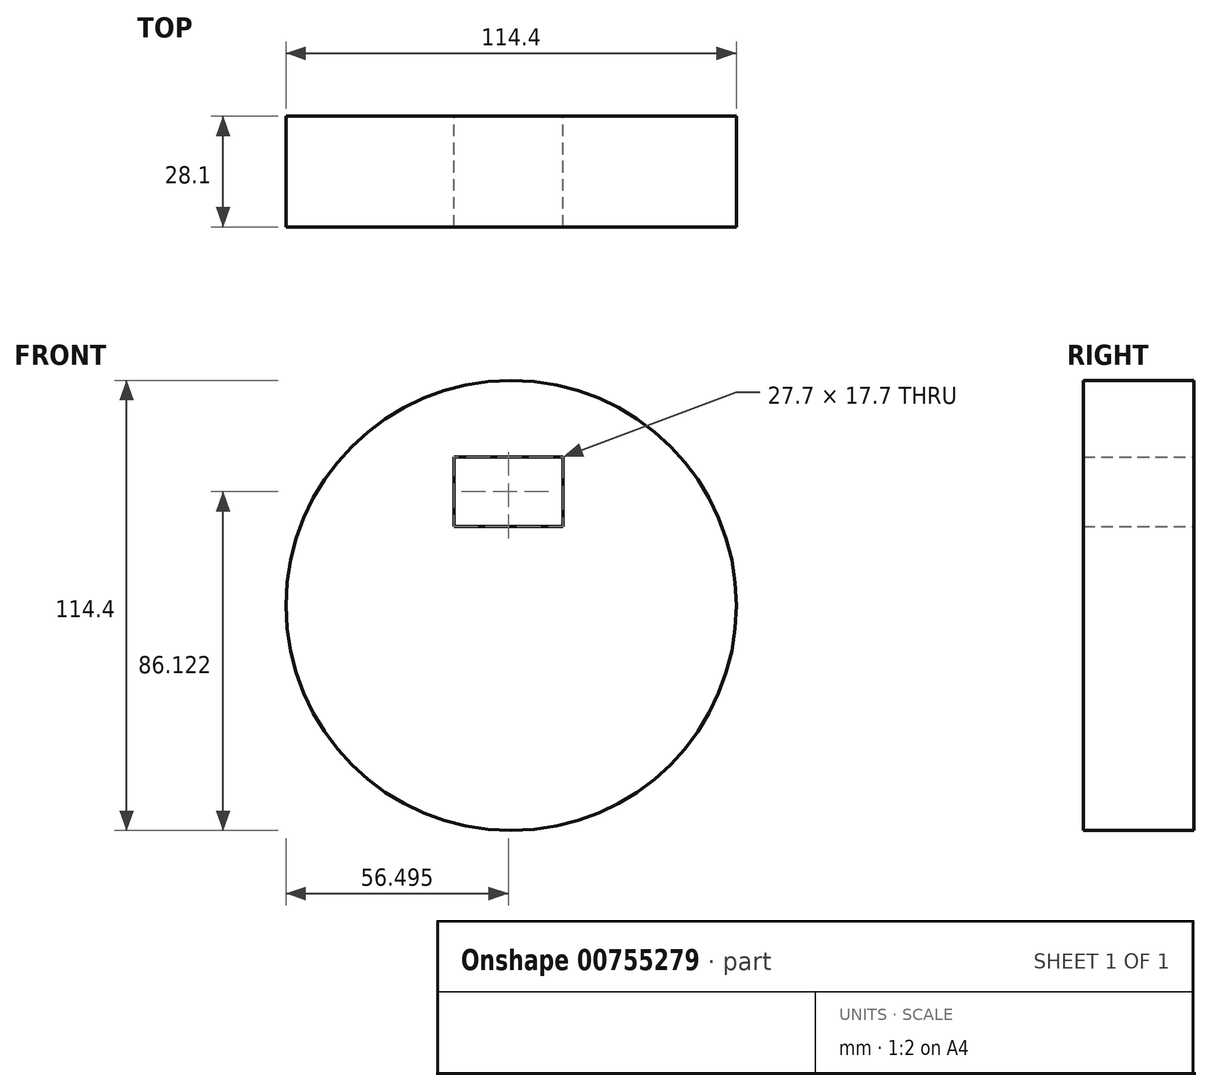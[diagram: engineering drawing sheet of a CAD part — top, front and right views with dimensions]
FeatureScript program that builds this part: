
annotation { "Feature Type Name" : "Feature", "Feature Type Description" : "" }
export const myFeature = defineFeature(function(context is Context, id is Id, definition is map)
    precondition{}
    {
        {
            var Q0;
            Q0=qCreatedBy(makeId("Front.planeOp"),FACE);
            var sketch = newSketch(context, id + "F0", { "sketchPlane" : qUnion([Q0])});
            skCircle(sketch, "E0", {"center": v(0, 0) * mm, "radius": 57.2 * mm});
            skLineSegment(sketch, "E1.bottom", {"start": v(-14.56, 37.77) * mm, "end": v(13.15, 37.77) * mm});
            skLineSegment(sketch, "E1.top", {"start": v(-14.56, 20.07) * mm, "end": v(13.15, 20.07) * mm});
            skLineSegment(sketch, "E1.left", {"start": v(-14.56, 37.77) * mm, "end": v(-14.56, 20.07) * mm});
            skLineSegment(sketch, "E1.right", {"start": v(13.15, 37.77) * mm, "end": v(13.15, 20.07) * mm});
            skLineSegment(sketch, "E2.bottom", {"start": v(-9.3, 20.07) * mm, "end": v(-13.53, 20.07) * mm});
            skLineSegment(sketch, "E2.top", {"start": v(-9.3, 20.07) * mm, "end": v(-13.53, 20.07) * mm});
            skLineSegment(sketch, "E2.left", {"start": v(-9.3, 20.07) * mm, "end": v(-9.3, 20.07) * mm});
            skLineSegment(sketch, "E2.right", {"start": v(-13.53, 20.07) * mm, "end": v(-13.53, 20.07) * mm});
            skSolve(sketch);
        }
        {
            var Q0;
            Q0=makeQuery(id+"F0.imprint","IMPRINT",FACE,{"disambiguationData":[TD([[makeQuery(id+"F0.imprint","IMPRINT",EDGE,{"derivedFrom":sQuery(id+"F0.wireOp",EDGE,"E0")}),1.0]])]});
            extrude(context, id + "F1", {"entities" : qUnion([Q0]), "depth" : 28.1 * mm, "offsetDistance" : 25 * mm});
        }
    });
